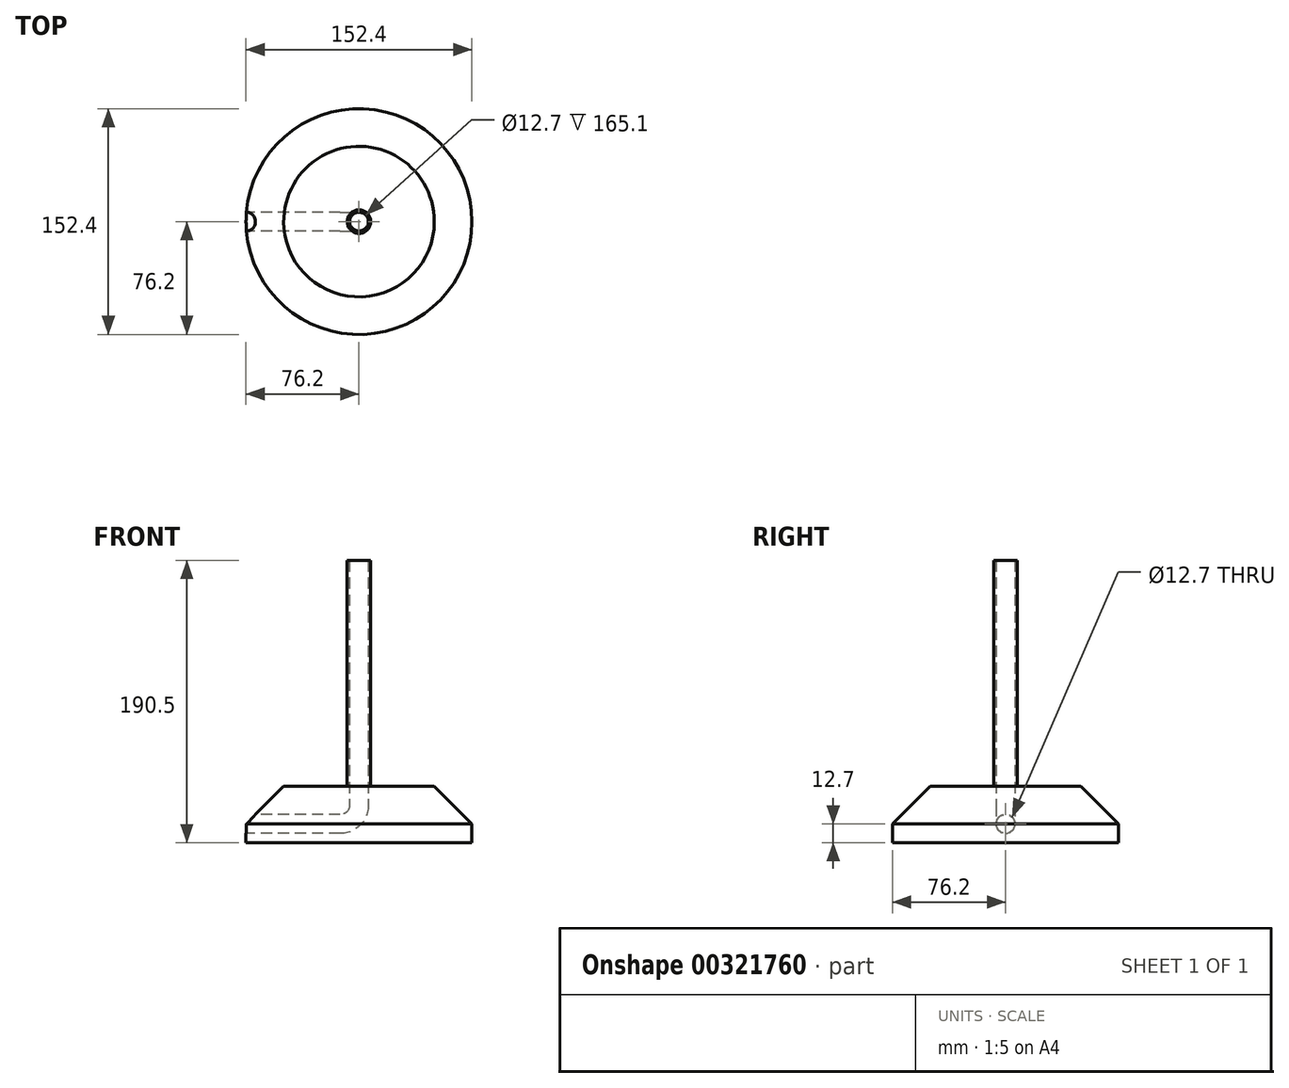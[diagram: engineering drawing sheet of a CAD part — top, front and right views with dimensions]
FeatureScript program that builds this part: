
annotation { "Feature Type Name" : "Feature", "Feature Type Description" : "" }
export const myFeature = defineFeature(function(context is Context, id is Id, definition is map)
    precondition{}
    {
        {
            var Q0;
            Q0=qCreatedBy(makeId("Top.planeOp"),FACE);
            var sketch = newSketch(context, id + "F0", { "sketchPlane" : qUnion([Q0])});
            skCircle(sketch, "E0", {"center": v(0, 0) * mm, "radius": 76.2 * mm});
            skSolve(sketch);
        }
        {
            var Q0;
            Q0=qCreatedBy(makeId("Top.planeOp"),FACE);
            cPlane(context, id + "F1", {"entities" : qUnion([Q0]), "cplaneType" : CPlaneType.OFFSET, "offset" : 25.4 * mm, "width" : 152.4 * mm, "height" : 152.4 * mm});
        }
        {
            var Q0;
            Q0=qCreatedBy(id+"F1.planeOp",FACE);
            var sketch = newSketch(context, id + "F2", { "sketchPlane" : qUnion([Q0])});
            skCircle(sketch, "E1", {"center": v(0, 0) * mm, "radius": 50.8 * mm});
            skSolve(sketch);
        }
        {
            var Q0;
            Q0=makeQuery(id+"F0.imprint","IMPRINT",FACE,{"disambiguationData":[TD([[makeQuery(id+"F0.imprint","IMPRINT",EDGE,{"derivedFrom":sQuery(id+"F0.wireOp",EDGE,"E0")}),1.0]])]});
            var Q1;
            Q1 = qSketchRegion(id + "F2", true);
            loft(context, id + "F3", {"sheetProfilesArray" : [{ "sheetProfileEntities" : qUnion([Q0]) }, { "sheetProfileEntities" : qUnion([Q1]) }]});
        }
        {
            var Q0;
            Q0 = qSketchRegion(id + "F0", true);
            extrude(context, id + "F4", {"entities" : qUnion([Q0]), "operationType" : NewBodyOperationType.ADD, "oppositeDirection" : true, "depth" : 12.7 * mm});
        }
        {
            var Q0;
            Q0=makeQuery(id+"F3.opLoft","CAP_FACE",FACE,{"disambiguationData":[OSD([makeQuery(id+"F2.imprint","IMPRINT",FACE,{"disambiguationData":[TD([[makeQuery(id+"F2.imprint","IMPRINT",EDGE,{"derivedFrom":sQuery(id+"F2.wireOp",EDGE,"E1")}),1.0]])]})])],"isStart":true});
            var sketch = newSketch(context, id + "F5", { "sketchPlane" : qUnion([Q0])});
            skCircle(sketch, "E2", {"center": v(0, 0) * mm, "radius": 6.35 * mm});
            skSolve(sketch);
        }
        {
            var Q0;
            Q0=qCreatedBy(makeId("Front.planeOp"),FACE);
            var sketch = newSketch(context, id + "F6", { "sketchPlane" : qUnion([Q0])});
            skLineSegment(sketch, "E3", {"start": v(0, 25.4) * mm, "end": v(0, 12.7) * mm});
            skLineSegment(sketch, "E4", {"start": v(-12.7, 0) * mm, "end": v(-82.22, 0) * mm});
            skPoint(sketch, "E5.visualSharp", {"position": v(0, 0) * mm});
            skArc(sketch, "E5.filletArc", {"start": v(-12.7, 0) * mm, "mid": v(-3.72, 3.72) * mm, "end": v(0, 12.7) * mm});
            skSolve(sketch);
        }
        {
            var Q0;
            Q0 = qSketchRegion(id + "F5", true);
            var Q1;
            Q1 = qConstructionFilter(qBodyType(qCreatedBy(id + "F6" ,EDGE), BodyType.WIRE), ConstructionObject.NO);
            sweep(context, id + "F7", {"operationType" : NewBodyOperationType.REMOVE, "profiles" : qUnion([Q0]), "path" : qUnion([Q1])});
        }
        {
            var Q0;
            Q0=qCreatedBy(makeId("Front.planeOp"),FACE);
            var sketch = newSketch(context, id + "F8", { "sketchPlane" : qUnion([Q0])});
            skLineSegment(sketch, "E6", {"start": v(0, 0) * mm, "end": v(0, 177.8) * mm, "construction": true});
            skLineSegment(sketch, "E7.bottom", {"start": v(6.35, 25.4) * mm, "end": v(7.94, 25.4) * mm});
            skLineSegment(sketch, "E7.top", {"start": v(6.35, 177.8) * mm, "end": v(7.94, 177.8) * mm});
            skLineSegment(sketch, "E7.left", {"start": v(6.35, 25.4) * mm, "end": v(6.35, 177.8) * mm});
            skLineSegment(sketch, "E7.right", {"start": v(7.94, 25.4) * mm, "end": v(7.94, 177.8) * mm});
            skSolve(sketch);
        }
        {
            var Q0;
            Q0 = qSketchRegion(id + "F8", true);
            var Q1;
            Q1=sQuery(id+"F8.wireOp",EDGE,"E6");
            revolve(context, id + "F9", {"operationType" : NewBodyOperationType.ADD, "entities" : qUnion([Q0]), "axis" : qUnion([Q1]), "revolveType" : RevolveType.FULL});
        }
    });
